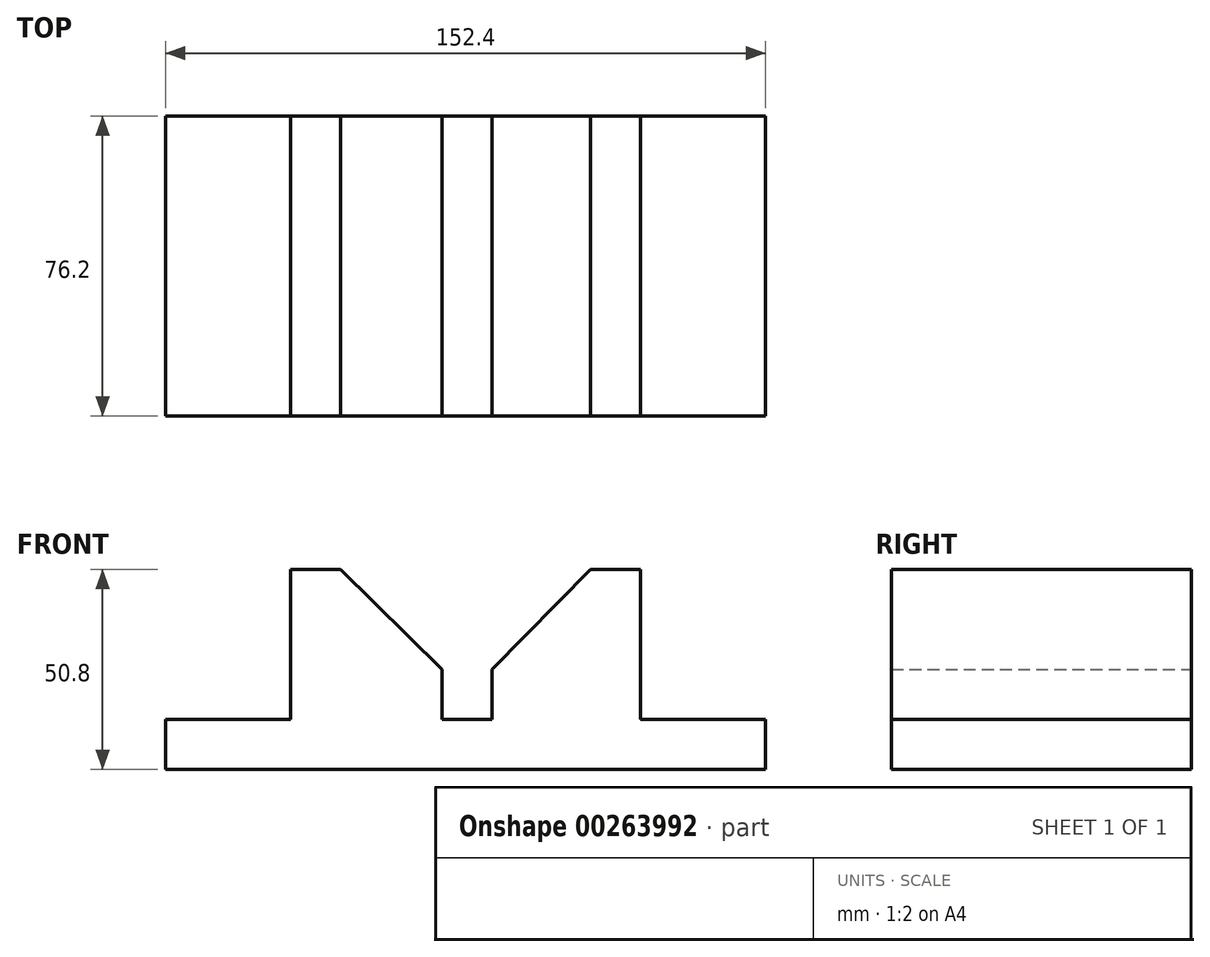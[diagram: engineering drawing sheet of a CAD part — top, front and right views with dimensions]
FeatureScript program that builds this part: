
annotation { "Feature Type Name" : "Feature", "Feature Type Description" : "" }
export const myFeature = defineFeature(function(context is Context, id is Id, definition is map)
    precondition{}
    {
        {
            var Q0;
            Q0=qCreatedBy(makeId("Front.planeOp"),FACE);
            var sketch = newSketch(context, id + "F0", { "sketchPlane" : qUnion([Q0])});
            skLineSegment(sketch, "E0", {"start": v(-76.56, 0) * mm, "end": v(-44.8, 0) * mm});
            skLineSegment(sketch, "E1", {"start": v(-44.8, 0) * mm, "end": v(-44.8, 38.1) * mm});
            skLineSegment(sketch, "E2", {"start": v(-44.8, 38.1) * mm, "end": v(-32.1, 38.1) * mm});
            skLineSegment(sketch, "E3", {"start": v(-76.56, 0) * mm, "end": v(-76.56, -12.7) * mm});
            skLineSegment(sketch, "E4", {"start": v(-76.56, -12.7) * mm, "end": v(75.84, -12.7) * mm});
            skLineSegment(sketch, "E5", {"start": v(75.84, -12.7) * mm, "end": v(75.84, 0) * mm});
            skLineSegment(sketch, "E6", {"start": v(75.84, 0) * mm, "end": v(44.1, 0) * mm});
            skLineSegment(sketch, "E7", {"start": v(44.1, 0) * mm, "end": v(44.1, 38.1) * mm});
            skLineSegment(sketch, "E8", {"start": v(44.1, 38.1) * mm, "end": v(31.4, 38.1) * mm});
            skPoint(sketch, "E9.start.orphan", {"position": v(-15.54, 18.85) * mm});
            skPoint(sketch, "E10.end.orphan", {"position": v(-2.84, 18.85) * mm});
            skLineSegment(sketch, "E11", {"start": v(0, 0) * mm, "end": v(-6.35, 0) * mm});
            skLineSegment(sketch, "E12", {"start": v(-6.35, 0) * mm, "end": v(0, 0) * mm});
            skLineSegment(sketch, "E13", {"start": v(0, 0) * mm, "end": v(6.35, 0) * mm});
            skLineSegment(sketch, "E14", {"start": v(6.35, 0) * mm, "end": v(6.35, 12.7) * mm});
            skLineSegment(sketch, "E15", {"start": v(-6.35, 0) * mm, "end": v(-6.35, 12.7) * mm});
            skLineSegment(sketch, "E16", {"start": v(-6.35, 12.7) * mm, "end": v(-32.1, 38.1) * mm});
            skLineSegment(sketch, "E17", {"start": v(6.35, 12.7) * mm, "end": v(31.4, 38.1) * mm});
            skSolve(sketch);
        }
        {
            var Q0;
            Q0=makeQuery(id+"F0.imprint","IMPRINT",FACE,{"disambiguationData":[TD([[makeQuery(id+"F0.imprint","IMPRINT",EDGE,{"derivedFrom":sQuery(id+"F0.wireOp",EDGE,"E0")}),-1.0]])]});
            extrude(context, id + "F1", {"entities" : qUnion([Q0]), "depth" : 76.2 * mm});
        }
    });
